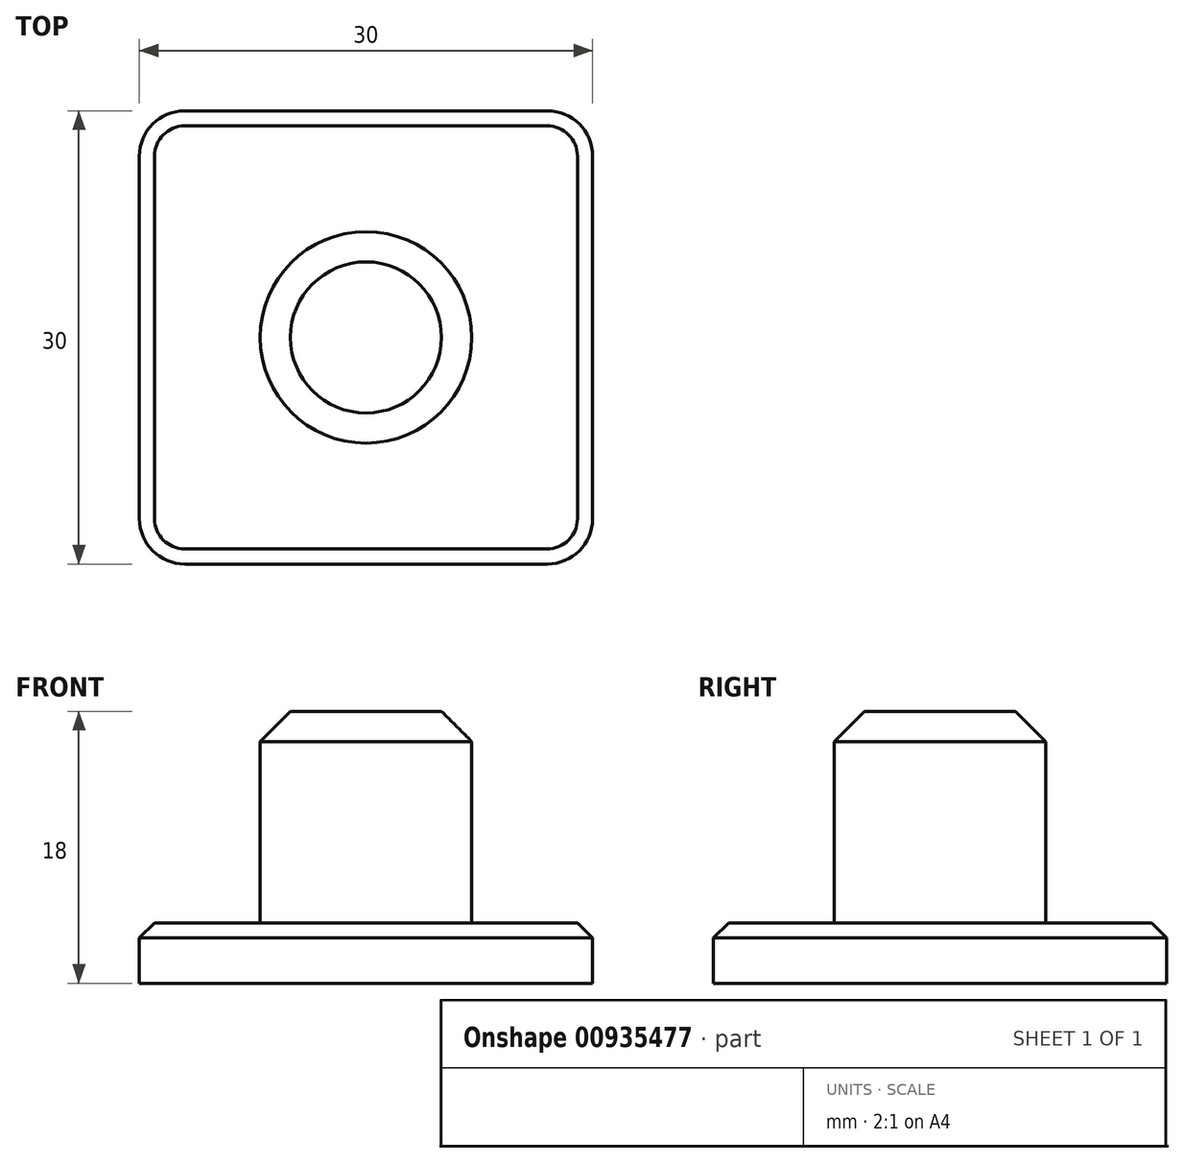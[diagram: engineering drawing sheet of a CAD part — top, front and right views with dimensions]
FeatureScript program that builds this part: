
annotation { "Feature Type Name" : "Feature", "Feature Type Description" : "" }
export const myFeature = defineFeature(function(context is Context, id is Id, definition is map)
    precondition{}
    {
        {
            var Q0;
            Q0=qCreatedBy(makeId("Top.planeOp"),FACE);
            var sketch = newSketch(context, id + "F0", { "sketchPlane" : qUnion([Q0])});
            skLineSegment(sketch, "E0.bottom", {"start": v(-15, -15) * mm, "end": v(15, -15) * mm});
            skLineSegment(sketch, "E0.top", {"start": v(-15, 15) * mm, "end": v(15, 15) * mm});
            skLineSegment(sketch, "E0.left", {"start": v(-15, -15) * mm, "end": v(-15, 15) * mm});
            skLineSegment(sketch, "E0.right", {"start": v(15, -15) * mm, "end": v(15, 15) * mm});
            skPoint(sketch, "E0.middle", {"position": v(0, 0) * mm});
            skSolve(sketch);
        }
        {
            var Q0;
            Q0=makeQuery(id+"F0.imprint","IMPRINT",FACE,{"disambiguationData":[TD([[makeQuery(id+"F0.imprint","IMPRINT",EDGE,{"derivedFrom":sQuery(id+"F0.wireOp",EDGE,"E0.bottom")}),1.0]])]});
            extrude(context, id + "F1", {"entities" : qUnion([Q0]), "depth" : 4 * mm, "offsetDistance" : 25 * mm});
        }
        {
            var Q0;
            Q0=makeQuery(id+"F1.opExtrude","SWEPT_EDGE",EDGE,{"disambiguationData":[OSD([sQuery(id+"F0.wireOp",EDGE,"E0.top"),sQuery(id+"F0.wireOp",EDGE,"E0.right")])]});
            var Q1;
            Q1=makeQuery(id+"F1.opExtrude","SWEPT_EDGE",EDGE,{"disambiguationData":[OSD([sQuery(id+"F0.wireOp",EDGE,"E0.top"),sQuery(id+"F0.wireOp",EDGE,"E0.left")])]});
            var Q2;
            Q2=makeQuery(id+"F1.opExtrude","SWEPT_EDGE",EDGE,{"disambiguationData":[OSD([sQuery(id+"F0.wireOp",EDGE,"E0.bottom"),sQuery(id+"F0.wireOp",EDGE,"E0.left")])]});
            var Q3;
            Q3=makeQuery(id+"F1.opExtrude","SWEPT_EDGE",EDGE,{"disambiguationData":[OSD([sQuery(id+"F0.wireOp",EDGE,"E0.bottom"),sQuery(id+"F0.wireOp",EDGE,"E0.right")])]});
            fillet(context, id + "F2", {"entities" : qUnion([Q0, Q1, Q2, Q3]), "radius" : 3 * mm, "tangentPropagation" : true, "allowEdgeOverflow" : false});
        }
        {
            var Q0;
            Q0=makeQuery(id+"F1.opExtrude","CAP_FACE",FACE,{"disambiguationData":[OSD([sQuery(id+"F0.wireOp",EDGE,"E0.bottom"),sQuery(id+"F0.wireOp",EDGE,"E0.top"),sQuery(id+"F0.wireOp",EDGE,"E0.left"),sQuery(id+"F0.wireOp",EDGE,"E0.right")])],"isStart":false});
            var sketch = newSketch(context, id + "F3", { "sketchPlane" : qUnion([Q0])});
            skCircle(sketch, "E1", {"center": v(0, 0) * mm, "radius": 7 * mm});
            skSolve(sketch);
        }
        {
            var Q0;
            Q0=makeQuery(id+"F3.imprint","IMPRINT",FACE,{"disambiguationData":[TD([[makeQuery(id+"F3.imprint","IMPRINT",EDGE,{"derivedFrom":sQuery(id+"F3.wireOp",EDGE,"E1")}),1.0]])]});
            extrude(context, id + "F4", {"entities" : qUnion([Q0]), "operationType" : NewBodyOperationType.ADD, "depth" : 14 * mm, "offsetDistance" : 25 * mm});
        }
        {
            var Q0;
            Q0=makeQuery(id+"F4.opExtrude","CAP_EDGE",EDGE,{"disambiguationData":[OSD([sQuery(id+"F3.wireOp",EDGE,"E1")])],"isStart":false});
            var Q1;
            Q1=makeQuery(id+"F4.opExtrude","CAP_EDGE",EDGE,{"disambiguationData":[OSD([sQuery(id+"F3.wireOp",EDGE,"E1")])],"isStart":true});
            chamfer(context, id + "F5", {"entities" : qUnion([Q0, Q1]), "width" : 2 * mm, "tangentPropagation" : true});
        }
        {
            var Q0;
            Q0=makeQuery(id+"F1.opExtrude","CAP_EDGE",EDGE,{"disambiguationData":[OSD([sQuery(id+"F0.wireOp",EDGE,"E0.bottom")])],"isStart":false});
            chamfer(context, id + "F6", {"entities" : qUnion([Q0]), "width" : 1 * mm, "tangentPropagation" : true});
        }
    });
